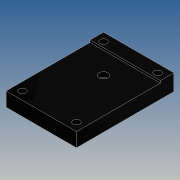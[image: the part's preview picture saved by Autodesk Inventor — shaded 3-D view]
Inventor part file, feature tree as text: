
AUTODESK INVENTOR PART (.ipt)
format: ipt  version: 2015 SP1 (Build 190203100, 203)  size: 235,008 bytes
history: native  units: mm
features: sketch x4, extrude x2, hole x2, pattern_linear x1, projected_geometry x1
ambient origin geometry x8: Origin, YZ Plane, XZ Plane, XY Plane, X Axis, Y Axis, Z Axis, Center Point
bodies: Solid1 (feature_tree)
feature tree (10):
  extrude  "Extrusion1"  Depth=15.0mm TaperAngle=0.0deg
  hole  "Hole1"  [1 undecoded]
  hole  "Hole2"  [1 undecoded]
  pattern_linear  "Rectangular Pattern2"  Spacing1=57.5mm  [1 undecoded]
  extrude  "Extrusion2"  Depth=2.0mm
  sketch  "Sketch1"  dims[d0=65.0mm d3=15.0mm d4=0.0mm]
  sketch  "Sketch2"  dims[d8=8.2mm d9=6.0mm d10=15.0mm d11=8.5mm d12=90.0deg d13=8.0mm d14=20.594885mm d16=25.0mm]
  sketch  "Sketch3"  dims[d17=25.0mm]
  sketch  "Sketch4"  dims[d18=6.3mm d19=6.0mm d20=11.0mm d21=7.0mm d22=90.0deg d23=8.0mm d24=20.594885mm d28=32.5mm d29=57.5mm d36=20.0mm d38=50.0mm d39=20.0mm d41=75.0mm d42=20.0mm d43=2.0mm d44=0.0mm]
  projected_geometry  "Project Cut Edges1"
note: 3 required parameter values undecoded (feature->parameter linkage not recoverable at this tier; creation-order binding heuristic only, values carry confidence <= 0.55)
